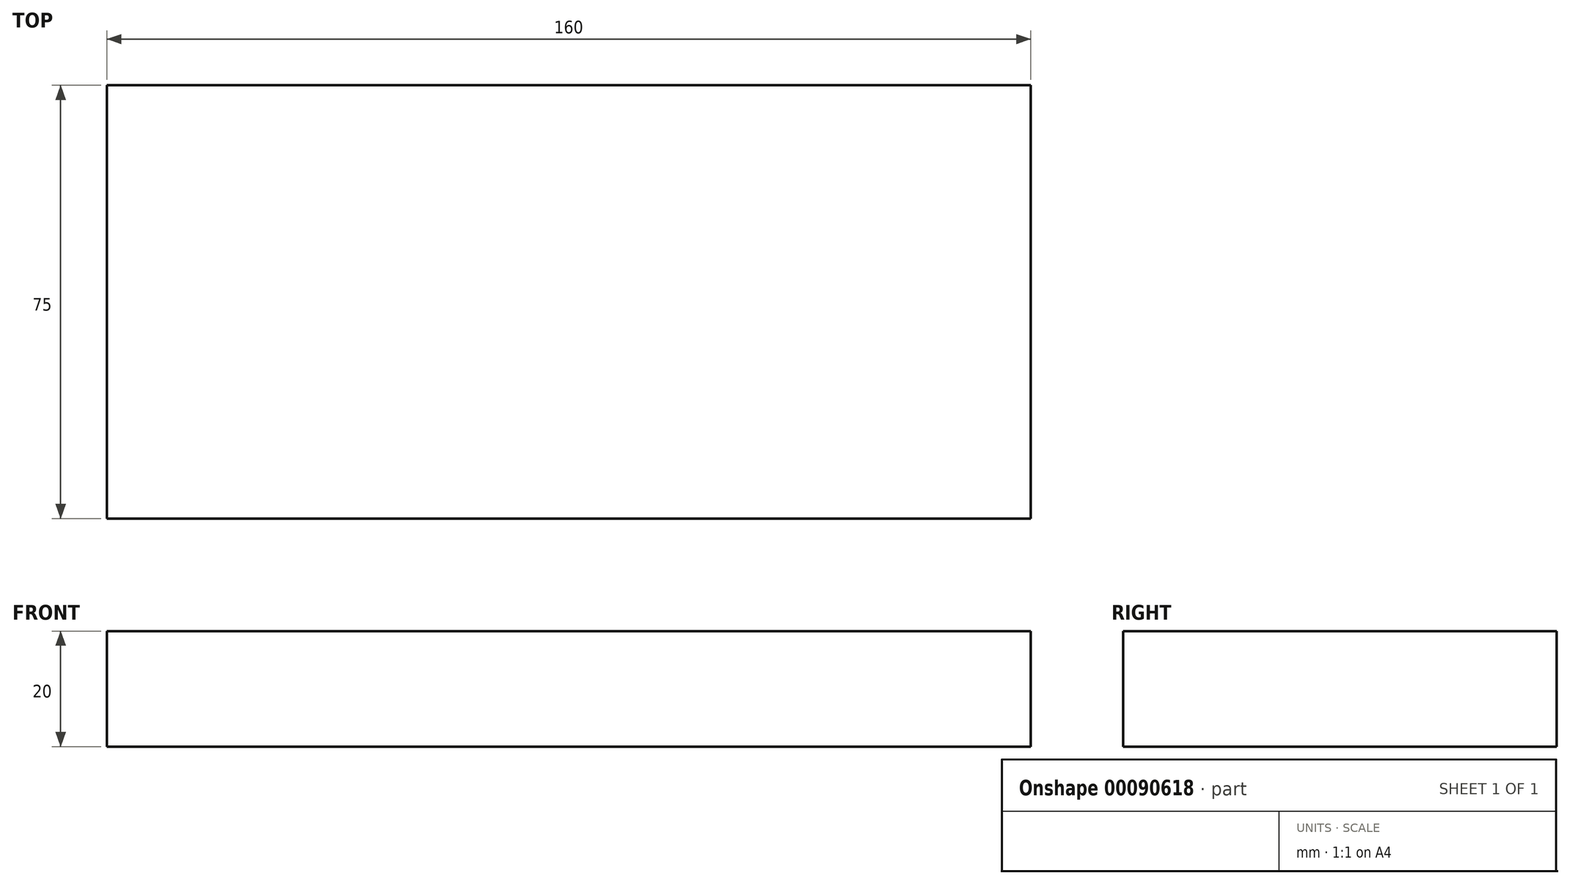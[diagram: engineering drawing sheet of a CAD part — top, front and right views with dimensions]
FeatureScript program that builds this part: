
annotation { "Feature Type Name" : "Feature", "Feature Type Description" : "" }
export const myFeature = defineFeature(function(context is Context, id is Id, definition is map)
    precondition{}
    {
        {
            var Q0;
            Q0=qCreatedBy(makeId("Top.planeOp"),FACE);
            var sketch = newSketch(context, id + "F0", { "sketchPlane" : qUnion([Q0])});
            skLineSegment(sketch, "E0.bottom", {"start": v(-63.77, 37.48) * mm, "end": v(96.23, 37.48) * mm});
            skLineSegment(sketch, "E0.top", {"start": v(-63.77, -37.52) * mm, "end": v(96.23, -37.52) * mm});
            skLineSegment(sketch, "E0.left", {"start": v(-63.77, 37.48) * mm, "end": v(-63.77, -37.52) * mm});
            skLineSegment(sketch, "E0.right", {"start": v(96.23, 37.48) * mm, "end": v(96.23, -37.52) * mm});
            skSolve(sketch);
        }
        {
            var Q0;
            Q0=makeQuery(id+"F0.imprint","IMPRINT",FACE,{"disambiguationData":[TD([[makeQuery(id+"F0.imprint","IMPRINT",EDGE,{"derivedFrom":sQuery(id+"F0.wireOp",EDGE,"E0.bottom")}),-1.0]])]});
            extrude(context, id + "F1", {"entities" : qUnion([Q0]), "depth" : 20 * mm});
        }
    });
